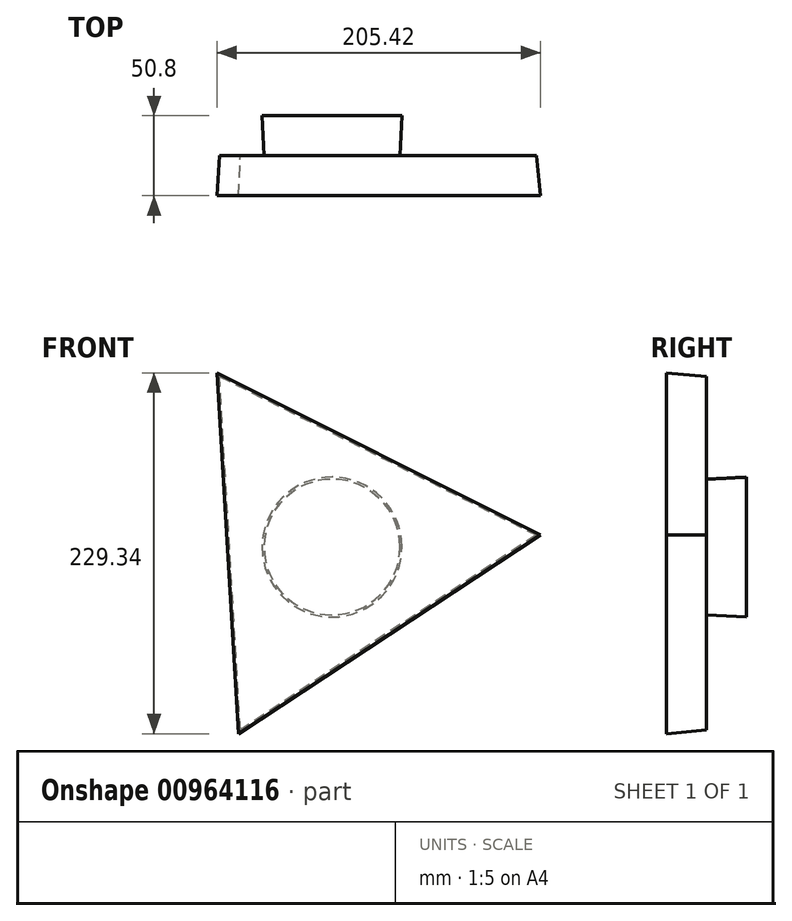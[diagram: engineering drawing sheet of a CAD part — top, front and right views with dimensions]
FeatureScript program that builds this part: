
annotation { "Feature Type Name" : "Feature", "Feature Type Description" : "" }
export const myFeature = defineFeature(function(context is Context, id is Id, definition is map)
    precondition{}
    {
        {
            var Q0;
            Q0=qCreatedBy(makeId("Front.planeOp"),FACE);
            var sketch = newSketch(context, id + "F0", { "sketchPlane" : qUnion([Q0])});
            skCircle(sketch, "E0.cCircle", {"center": v(0, 0) * mm, "radius": 65 * mm, "construction": true});
            skLineSegment(sketch, "E0.0", {"start": v(-71.55, 108.52) * mm, "end": v(129.76, 7.7) * mm});
            skLineSegment(sketch, "E0.1", {"start": v(129.76, 7.7) * mm, "end": v(-58.2, -116.22) * mm});
            skLineSegment(sketch, "E0.2", {"start": v(-58.2, -116.22) * mm, "end": v(-71.55, 108.52) * mm});
            skPoint(sketch, "E0.0.midPoint", {"position": v(29.1, 58.11) * mm});
            skSolve(sketch);
        }
        {
            var Q0;
            Q0 = qSketchRegion(id + "F0", true);
            extrude(context, id + "F1", {"entities" : qUnion([Q0]), "depth" : 25.4 * mm, "offsetDistance" : 25.4 * mm, "hasDraft" : true, "draftAngle" : 3 * degree});
        }
        {
            var Q0;
            Q0=makeQuery(id+"F1.opExtrude","CAP_FACE",FACE,{"disambiguationData":[OSD([sQuery(id+"F0.wireOp",EDGE,"E0.0"),sQuery(id+"F0.wireOp",EDGE,"E0.1"),sQuery(id+"F0.wireOp",EDGE,"E0.2")])],"isStart":true});
            var sketch = newSketch(context, id + "F2", { "sketchPlane" : qUnion([Q0])});
            skCircle(sketch, "E1", {"center": v(0, 0) * mm, "radius": 43.11 * mm});
            skSolve(sketch);
        }
        {
            var Q0;
            Q0 = qSketchRegion(id + "F2", true);
            extrude(context, id + "F3", {"entities" : qUnion([Q0]), "operationType" : NewBodyOperationType.ADD, "depth" : 25.4 * mm, "offsetDistance" : 25.4 * mm, "hasDraft" : true, "draftAngle" : 3 * degree});
        }
        {
            var Q0;
            Q0=makeQuery(id+"F1.opExtrude","CAP_FACE",FACE,{"disambiguationData":[OSD([sQuery(id+"F0.wireOp",EDGE,"E0.0"),sQuery(id+"F0.wireOp",EDGE,"E0.1"),sQuery(id+"F0.wireOp",EDGE,"E0.2")])],"isStart":true});
            var sketch = newSketch(context, id + "F4", { "sketchPlane" : qUnion([Q0])});
            skCircle(sketch, "E2", {"center": v(0, 0) * mm, "radius": 16.68 * mm});
            skSolve(sketch);
        }
        {
            var Q0;
            Q0 = qSketchRegion(id + "F4", true);
            extrude(context, id + "F5", {"entities" : qUnion([Q0]), "operationType" : NewBodyOperationType.ADD, "depth" : 25.4 * mm, "offsetDistance" : 25.4 * mm, "hasDraft" : true, "draftAngle" : 3 * degree});
        }
    });
